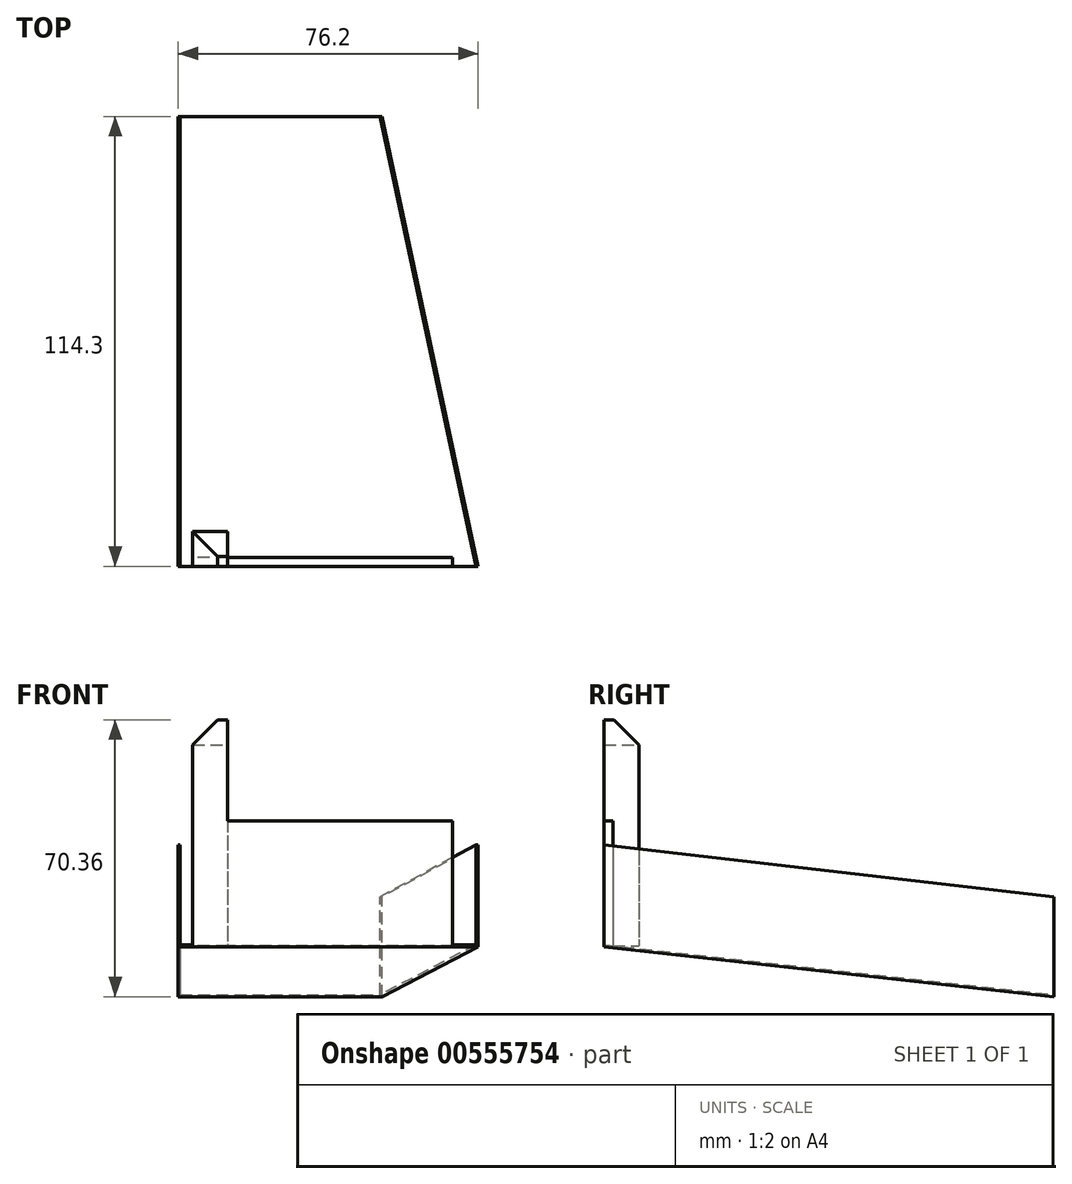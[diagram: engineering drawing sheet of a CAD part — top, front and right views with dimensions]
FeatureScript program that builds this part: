
annotation { "Feature Type Name" : "Feature", "Feature Type Description" : "" }
export const myFeature = defineFeature(function(context is Context, id is Id, definition is map)
    precondition{}
    {
        {
            var Q0;
            Q0=qCreatedBy(makeId("Front.planeOp"),FACE);
            var sketch = newSketch(context, id + "F0", { "sketchPlane" : qUnion([Q0])});
            skLineSegment(sketch, "E0.bottom", {"start": v(0, 0) * mm, "end": v(0.5, 0) * mm});
            skLineSegment(sketch, "E0.left", {"start": v(0, 0) * mm, "end": v(0, -24.9) * mm});
            skLineSegment(sketch, "E0.right", {"start": v(0.5, 0) * mm, "end": v(0.5, -24.9) * mm});
            skLineSegment(sketch, "E1.bottom", {"start": v(0.5, -24.9) * mm, "end": v(51.3, -24.9) * mm});
            skLineSegment(sketch, "E1.top", {"start": v(0, -25.4) * mm, "end": v(51.82, -25.4) * mm});
            skLineSegment(sketch, "E1.left", {"start": v(0, -24.9) * mm, "end": v(0, -25.4) * mm});
            skLineSegment(sketch, "E1.right", {"start": v(51.82, -24.9) * mm, "end": v(51.82, -25.4) * mm});
            skLineSegment(sketch, "E2.top", {"start": v(51.82, 0) * mm, "end": v(51.3, 0) * mm});
            skLineSegment(sketch, "E2.left", {"start": v(51.82, -24.9) * mm, "end": v(51.82, 0) * mm});
            skLineSegment(sketch, "E2.right", {"start": v(51.3, -24.9) * mm, "end": v(51.3, 0) * mm});
            skSolve(sketch);
        }
        {
            var Q0;
            Q0=qCreatedBy(makeId("Front.planeOp"),FACE);
            cPlane(context, id + "F1", {"entities" : qUnion([Q0]), "cplaneType" : CPlaneType.OFFSET, "offset" : 114.3 * mm, "width" : 152.4 * mm, "height" : 152.4 * mm});
        }
        {
            var Q0;
            Q0=qCreatedBy(id+"F1.planeOp",FACE);
            var sketch = newSketch(context, id + "F2", { "sketchPlane" : qUnion([Q0])});
            skLineSegment(sketch, "E3.bottom", {"start": v(0, 13.2) * mm, "end": v(0.5, 13.2) * mm});
            skLineSegment(sketch, "E3.left", {"start": v(0, 13.2) * mm, "end": v(0, -12.2) * mm});
            skLineSegment(sketch, "E3.right", {"start": v(0.5, 13.2) * mm, "end": v(0.5, -12.2) * mm});
            skLineSegment(sketch, "E4.bottom", {"start": v(76.2, 13.2) * mm, "end": v(75.7, 13.2) * mm});
            skLineSegment(sketch, "E4.left", {"start": v(76.2, 13.2) * mm, "end": v(76.2, -12.2) * mm});
            skLineSegment(sketch, "E4.right", {"start": v(75.7, 13.2) * mm, "end": v(75.7, -12.2) * mm});
            skLineSegment(sketch, "E5.bottom", {"start": v(75.7, -12.2) * mm, "end": v(0.5, -12.2) * mm});
            skLineSegment(sketch, "E5.top", {"start": v(76.2, -12.7) * mm, "end": v(0, -12.7) * mm});
            skLineSegment(sketch, "E5.left", {"start": v(76.2, -12.2) * mm, "end": v(76.2, -12.7) * mm});
            skLineSegment(sketch, "E5.right", {"start": v(0, -12.2) * mm, "end": v(0, -12.7) * mm});
            skSolve(sketch);
        }
        {
            var Q0;
            Q0=makeQuery(id+"F2.imprint","IMPRINT",FACE,{"disambiguationData":[TD([[makeQuery(id+"F2.imprint","IMPRINT",EDGE,{"derivedFrom":sQuery(id+"F2.wireOp",EDGE,"E3.bottom")}),-1.0]])]});
            var Q1;
            Q1=makeQuery(id+"F0.imprint","IMPRINT",FACE,{"disambiguationData":[TD([[makeQuery(id+"F0.imprint","IMPRINT",EDGE,{"derivedFrom":sQuery(id+"F0.wireOp",EDGE,"E0.bottom")}),-1.0]])]});
            loft(context, id + "F3", {"sheetProfilesArray" : [{ "sheetProfileEntities" : qUnion([Q0]) }, { "sheetProfileEntities" : qUnion([Q1]) }]});
        }
        {
            var Q0;
            Q0=makeQuery(id+"F3.opLoft","MID_CAP_EDGE",EDGE,{"disambiguationData":[OSD([sQuery(id+"F2.wireOp",EDGE,"E3.right"),sQuery(id+"F2.wireOp",EDGE,"E4.right"),sQuery(id+"F2.wireOp",EDGE,"E5.bottom")])],"capPos":0.0});
            cPlane(context, id + "F4", {"entities" : qUnion([Q0]), "cplaneType" : CPlaneType.LINE_ANGLE, "offset" : 25.4 * mm, "angle" : 90 * degree, "width" : 152.4 * mm, "height" : 152.4 * mm});
        }
        {
            var Q0;
            Q0=qCreatedBy(id+"F4.planeOp",FACE);
            var sketch = newSketch(context, id + "F5", { "sketchPlane" : qUnion([Q0])});
            skLineSegment(sketch, "E6.bottom", {"start": v(3.68, -114.3) * mm, "end": v(12.57, -114.3) * mm});
            skLineSegment(sketch, "E6.top", {"start": v(3.68, -105.41) * mm, "end": v(12.57, -105.41) * mm});
            skLineSegment(sketch, "E6.left", {"start": v(3.68, -114.3) * mm, "end": v(3.68, -105.41) * mm});
            skLineSegment(sketch, "E6.right", {"start": v(12.57, -114.3) * mm, "end": v(12.57, -105.41) * mm});
            skSolve(sketch);
        }
        {
            var Q0;
            Q0=makeQuery(id+"F5.imprint","IMPRINT",FACE,{"disambiguationData":[TD([[makeQuery(id+"F5.imprint","IMPRINT",EDGE,{"derivedFrom":sQuery(id+"F5.wireOp",EDGE,"E6.bottom")}),1.0]])]});
            extrude(context, id + "F6", {"entities" : qUnion([Q0]), "operationType" : NewBodyOperationType.ADD, "depth" : 57.15 * mm, "offsetDistance" : 25.4 * mm});
        }
        {
            var Q0;
            Q0=makeQuery(id+"F6.opExtrude","CAP_FACE",FACE,{"disambiguationData":[OSD([sQuery(id+"F5.wireOp",EDGE,"E6.bottom"),sQuery(id+"F5.wireOp",EDGE,"E6.top"),sQuery(id+"F5.wireOp",EDGE,"E6.left"),sQuery(id+"F5.wireOp",EDGE,"E6.right")])],"isStart":true});
            extrude(context, id + "F7", {"entities" : qUnion([Q0]), "operationType" : NewBodyOperationType.ADD, "depth" : 0.25 * mm, "offsetDistance" : 25.4 * mm});
        }
        {
            var Q0;
            {var subQ0=sQuery(id+"F5.wireOp",EDGE,"E6.right");Q0=makeQuery(id+"F7.boolean.opBoolean","MERGE",FACE,{"derivedFrom":[makeQuery(id+"F6.opExtrude","SWEPT_FACE",FACE,{"disambiguationData":[OSD([subQ0])]}),makeQuery(id+"F7.opExtrude","SWEPT_FACE",FACE,{"disambiguationData":[OSD([subQ0])]})]});}
            var sketch = newSketch(context, id + "F8", { "sketchPlane" : qUnion([Q0])});
            skLineSegment(sketch, "E7.bottom", {"start": v(-114.3, 19.3) * mm, "end": v(-112.01, 19.3) * mm});
            skLineSegment(sketch, "E7.top", {"start": v(-114.3, -12.45) * mm, "end": v(-112.01, -12.45) * mm});
            skLineSegment(sketch, "E7.left", {"start": v(-114.3, 19.3) * mm, "end": v(-114.3, -12.45) * mm});
            skLineSegment(sketch, "E7.right", {"start": v(-112.01, 19.3) * mm, "end": v(-112.01, -12.45) * mm});
            skSolve(sketch);
        }
        {
            var Q0;
            {var subQ0=sQuery(id+"F8.wireOp",EDGE,"E7.bottom");Q0=makeQuery(id+"F8.imprint","IMPRINT",FACE,{"disambiguationData":[TD([[makeQuery(id+"F8.imprint","IMPRINT",EDGE,{"derivedFrom":subQ0}),-1.0]])]});}
            extrude(context, id + "F9", {"entities" : qUnion([Q0]), "operationType" : NewBodyOperationType.ADD, "depth" : 57.15 * mm, "offsetDistance" : 25.4 * mm});
        }
        {
            var Q0;
            Q0=makeQuery(id+"F6.opExtrude","CAP_EDGE",EDGE,{"disambiguationData":[OSD([sQuery(id+"F5.wireOp",EDGE,"E6.left")])],"isStart":false});
            chamfer(context, id + "F10", {"entities" : qUnion([Q0]), "width" : 6.35 * mm, "tangentPropagation" : true});
        }
        {
            var Q0;
            Q0=makeQuery(id+"F6.opExtrude","CAP_EDGE",EDGE,{"disambiguationData":[OSD([sQuery(id+"F5.wireOp",EDGE,"E6.top")])],"isStart":false});
            chamfer(context, id + "F11", {"entities" : qUnion([Q0]), "width" : 6.35 * mm, "tangentPropagation" : true});
        }
    });
